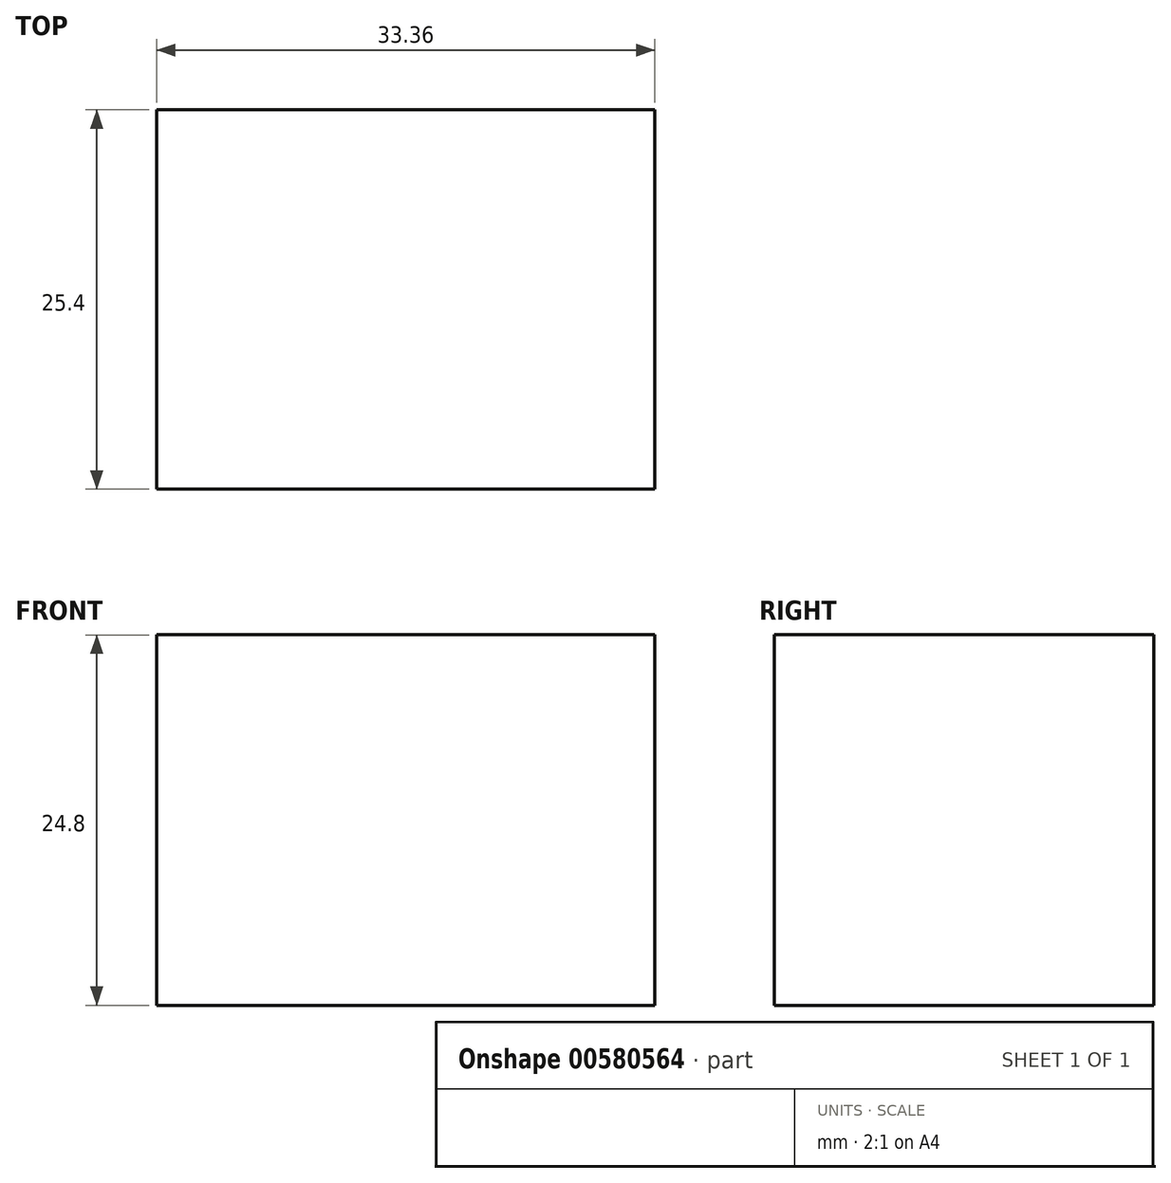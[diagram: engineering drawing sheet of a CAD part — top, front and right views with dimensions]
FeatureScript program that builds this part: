
annotation { "Feature Type Name" : "Feature", "Feature Type Description" : "" }
export const myFeature = defineFeature(function(context is Context, id is Id, definition is map)
    precondition{}
    {
        {
            var Q0;
            Q0=qCreatedBy(makeId("Front.planeOp"),FACE);
            var sketch = newSketch(context, id + "F0", { "sketchPlane" : qUnion([Q0])});
            skLineSegment(sketch, "E0.bottom", {"start": v(-16.68, 12.4) * mm, "end": v(16.68, 12.4) * mm});
            skLineSegment(sketch, "E0.top", {"start": v(-16.68, -12.4) * mm, "end": v(16.68, -12.4) * mm});
            skLineSegment(sketch, "E0.left", {"start": v(-16.68, 12.4) * mm, "end": v(-16.68, -12.4) * mm});
            skLineSegment(sketch, "E0.right", {"start": v(16.68, 12.4) * mm, "end": v(16.68, -12.4) * mm});
            skPoint(sketch, "E0.middle", {"position": v(0, 0) * mm});
            skSolve(sketch);
        }
        {
            var Q0;
            Q0=makeQuery(id+"F0.imprint","IMPRINT",FACE,{"disambiguationData":[TD([[makeQuery(id+"F0.imprint","IMPRINT",EDGE,{"derivedFrom":sQuery(id+"F0.wireOp",EDGE,"E0.bottom")}),-1.0]])]});
            extrude(context, id + "F1", {"entities" : qUnion([Q0]), "depth" : 25.4 * mm, "offsetDistance" : 25.4 * mm});
        }
    });
